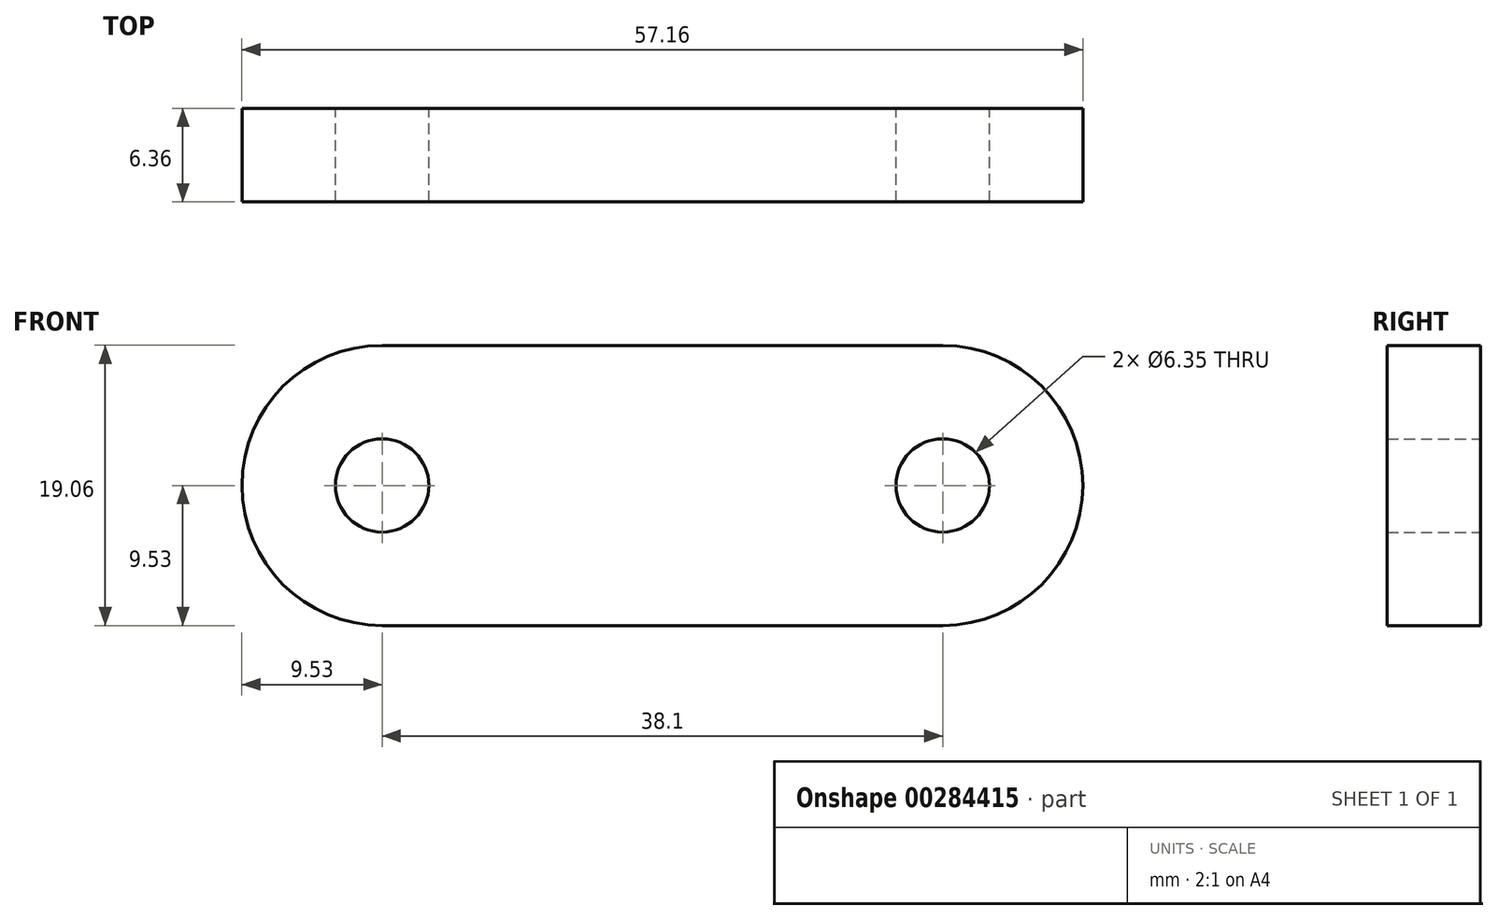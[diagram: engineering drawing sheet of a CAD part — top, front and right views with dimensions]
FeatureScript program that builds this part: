
annotation { "Feature Type Name" : "Feature", "Feature Type Description" : "" }
export const myFeature = defineFeature(function(context is Context, id is Id, definition is map)
    precondition{}
    {
        {
            var Q0;
            Q0=qCreatedBy(makeId("Front.planeOp"),FACE);
            var sketch = newSketch(context, id + "F0", { "sketchPlane" : qUnion([Q0])});
            skLineSegment(sketch, "E0.bottom", {"start": v(19.05, -9.53) * mm, "end": v(-19.05, -9.53) * mm});
            skLineSegment(sketch, "E0.top", {"start": v(19.05, 9.53) * mm, "end": v(-19.05, 9.53) * mm});
            skPoint(sketch, "E0.middle", {"position": v(0, 0) * mm});
            skArc(sketch, "E1", {"start": v(-19.05, 9.53) * mm, "mid": v(-28.58, 0) * mm, "end": v(-19.05, -9.53) * mm});
            skArc(sketch, "E2", {"start": v(19.05, -9.53) * mm, "mid": v(28.58, 0) * mm, "end": v(19.05, 9.53) * mm});
            skCircle(sketch, "E3", {"center": v(-19.05, 0) * mm, "radius": 3.18 * mm});
            skCircle(sketch, "E4", {"center": v(19.05, 0) * mm, "radius": 3.18 * mm});
            skSolve(sketch);
        }
        {
            var Q0;
            Q0=makeQuery(id+"F0.imprint","IMPRINT",FACE,{"disambiguationData":[TD([[makeQuery(id+"F0.imprint","IMPRINT",EDGE,{"derivedFrom":sQuery(id+"F0.wireOp",EDGE,"E0.bottom")}),-1.0]])]});
            extrude(context, id + "F1", {"entities" : qUnion([Q0]), "depth" : 6.35 * mm, "symmetric" : true});
        }
    });
